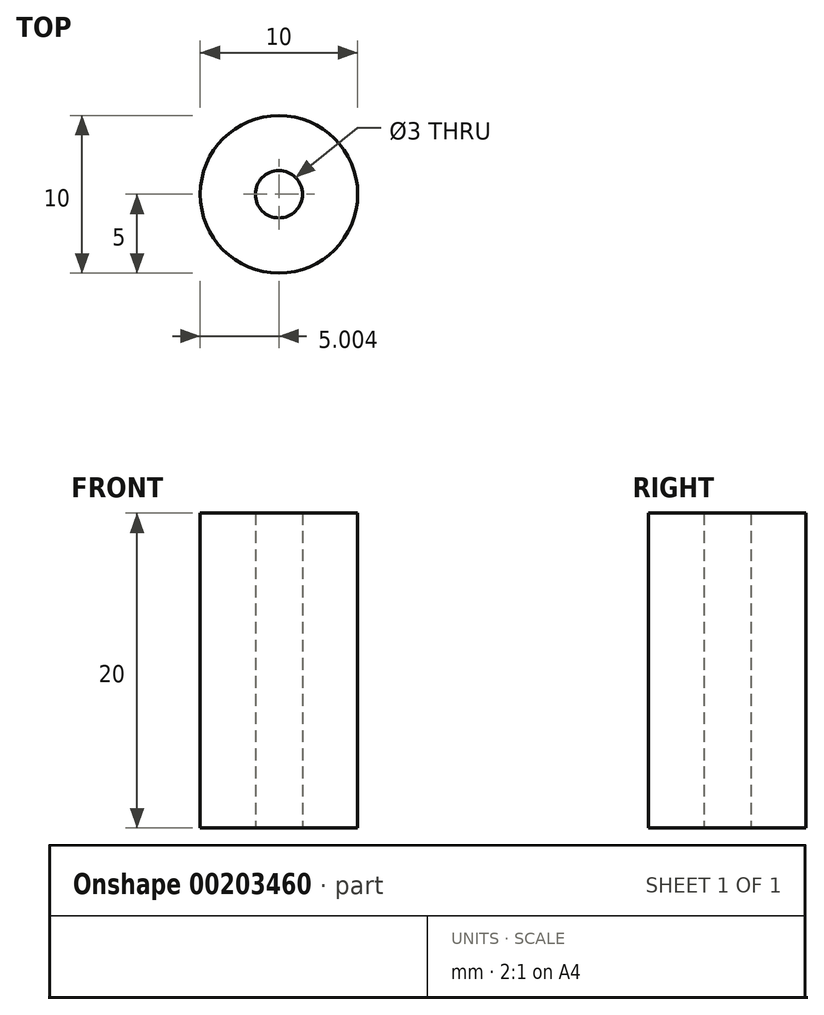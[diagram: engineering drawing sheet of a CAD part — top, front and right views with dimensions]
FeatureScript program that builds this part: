
annotation { "Feature Type Name" : "Feature", "Feature Type Description" : "" }
export const myFeature = defineFeature(function(context is Context, id is Id, definition is map)
    precondition{}
    {
        {
            var Q0;
            Q0=qCreatedBy(makeId("Top.planeOp"),FACE);
            var sketch = newSketch(context, id + "F0", { "sketchPlane" : qUnion([Q0])});
            skCircle(sketch, "E0", {"center": v(10.58, -6.24) * mm, "radius": 5 * mm});
            skCircle(sketch, "E1", {"center": v(10.58, -6.24) * mm, "radius": 1.5 * mm});
            skSolve(sketch);
        }
        {
            var Q0;
            Q0 = qSketchRegion(id + "F0", true);
            extrude(context, id + "F1", {"entities" : qUnion([Q0]), "depth" : 20 * mm});
        }
    });
